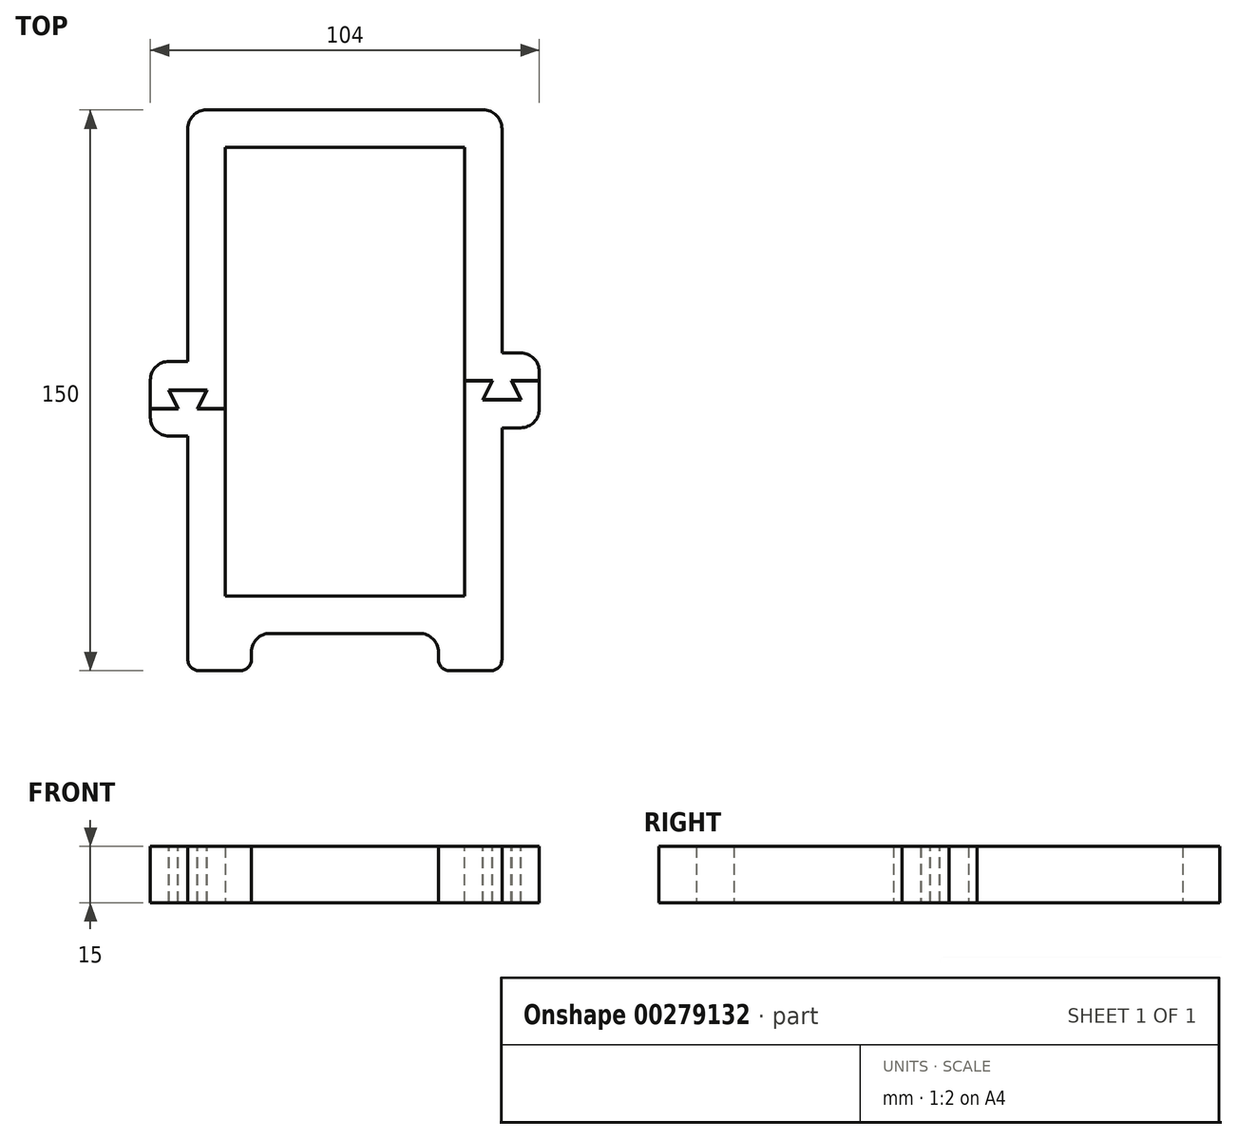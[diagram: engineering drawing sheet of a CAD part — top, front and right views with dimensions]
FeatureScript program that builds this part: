
annotation { "Feature Type Name" : "Feature", "Feature Type Description" : "" }
export const myFeature = defineFeature(function(context is Context, id is Id, definition is map)
    precondition{}
    {
        {
            var Q0;
            Q0=qCreatedBy(makeId("Top.planeOp"),FACE);
            var sketch = newSketch(context, id + "F0", { "sketchPlane" : qUnion([Q0])});
            skLineSegment(sketch, "E0.bottom", {"start": v(42, 75) * mm, "end": v(-42, 75) * mm});
            skLineSegment(sketch, "E0.left", {"start": v(42, 75) * mm, "end": v(42, -75) * mm});
            skLineSegment(sketch, "E0.right", {"start": v(-42, 75) * mm, "end": v(-42, -75) * mm});
            skPoint(sketch, "E0.middle", {"position": v(0, 0) * mm});
            skLineSegment(sketch, "E1.bottom", {"start": v(-32, 65) * mm, "end": v(32, 65) * mm});
            skLineSegment(sketch, "E1.top", {"start": v(-32, -55) * mm, "end": v(32, -55) * mm});
            skLineSegment(sketch, "E1.left", {"start": v(-32, 65) * mm, "end": v(-32, -55) * mm});
            skLineSegment(sketch, "E1.right", {"start": v(32, 65) * mm, "end": v(32, -55) * mm});
            skLineSegment(sketch, "E2.top", {"start": v(-25, -65) * mm, "end": v(25, -65) * mm});
            skLineSegment(sketch, "E2.left", {"start": v(-25, -75) * mm, "end": v(-25, -65) * mm});
            skLineSegment(sketch, "E2.right", {"start": v(25, -75) * mm, "end": v(25, -65) * mm});
            skLineSegment(sketch, "E3", {"start": v(-42, -75) * mm, "end": v(-25, -75) * mm});
            skLineSegment(sketch, "E4", {"start": v(25, -75) * mm, "end": v(42, -75) * mm});
            skSolve(sketch);
        }
        {
            var Q0;
            Q0=makeQuery(id+"F0.imprint","IMPRINT",FACE,{"disambiguationData":[TD([[makeQuery(id+"F0.imprint","IMPRINT",EDGE,{"derivedFrom":sQuery(id+"F0.wireOp",EDGE,"E0.bottom")}),1.0]])]});
            extrude(context, id + "F1", {"entities" : qUnion([Q0]), "depth" : 15 * mm});
        }
        {
            var Q0;
            Q0=makeQuery(id+"F1.opExtrude","SWEPT_EDGE",EDGE,{"disambiguationData":[OSD([sQuery(id+"F0.wireOp",EDGE,"E2.right"),sQuery(id+"F0.wireOp",EDGE,"E4")])]});
            var Q1;
            Q1=makeQuery(id+"F1.opExtrude","SWEPT_EDGE",EDGE,{"disambiguationData":[OSD([sQuery(id+"F0.wireOp",EDGE,"E0.left"),sQuery(id+"F0.wireOp",EDGE,"E4")])]});
            var Q2;
            Q2=makeQuery(id+"F1.opExtrude","SWEPT_EDGE",EDGE,{"disambiguationData":[OSD([sQuery(id+"F0.wireOp",EDGE,"E2.left"),sQuery(id+"F0.wireOp",EDGE,"E3")])]});
            var Q3;
            Q3=makeQuery(id+"F1.opExtrude","SWEPT_EDGE",EDGE,{"disambiguationData":[OSD([sQuery(id+"F0.wireOp",EDGE,"E0.right"),sQuery(id+"F0.wireOp",EDGE,"E3")])]});
            fillet(context, id + "F2", {"entities" : qUnion([Q0, Q1, Q2, Q3]), "radius" : 3 * mm, "tangentPropagation" : true, "allowEdgeOverflow" : false});
        }
        {
            var Q0;
            Q0=makeQuery(id+"F1.opExtrude","SWEPT_EDGE",EDGE,{"disambiguationData":[OSD([sQuery(id+"F0.wireOp",EDGE,"E2.top"),sQuery(id+"F0.wireOp",EDGE,"E2.left")])]});
            var Q1;
            Q1=makeQuery(id+"F1.opExtrude","SWEPT_EDGE",EDGE,{"disambiguationData":[OSD([sQuery(id+"F0.wireOp",EDGE,"E2.top"),sQuery(id+"F0.wireOp",EDGE,"E2.right")])]});
            var Q2;
            Q2=makeQuery(id+"F1.opExtrude","SWEPT_EDGE",EDGE,{"disambiguationData":[OSD([sQuery(id+"F0.wireOp",EDGE,"E0.bottom"),sQuery(id+"F0.wireOp",EDGE,"E0.right")])]});
            var Q3;
            Q3=makeQuery(id+"F1.opExtrude","SWEPT_EDGE",EDGE,{"disambiguationData":[OSD([sQuery(id+"F0.wireOp",EDGE,"E0.bottom"),sQuery(id+"F0.wireOp",EDGE,"E0.left")])]});
            fillet(context, id + "F3", {"entities" : qUnion([Q0, Q1, Q2, Q3]), "radius" : 5 * mm, "tangentPropagation" : true, "allowEdgeOverflow" : false});
        }
        {
            var Q0;
            Q0=makeQuery(id+"F1.opExtrude","SWEPT_FACE",FACE,{"disambiguationData":[OSD([sQuery(id+"F0.wireOp",EDGE,"E0.right")])]});
            var sketch = newSketch(context, id + "F4", { "sketchPlane" : qUnion([Q0])});
            skLineSegment(sketch, "E5.bottom", {"start": v(12.24, 15) * mm, "end": v(-7.76, 15) * mm});
            skLineSegment(sketch, "E5.top", {"start": v(12.24, 0) * mm, "end": v(-7.76, 0) * mm});
            skLineSegment(sketch, "E5.left", {"start": v(12.24, 15) * mm, "end": v(12.24, 0) * mm});
            skLineSegment(sketch, "E5.right", {"start": v(-7.76, 15) * mm, "end": v(-7.76, 0) * mm});
            skSolve(sketch);
        }
        {
            var Q0;
            Q0=makeQuery(id+"F4.imprint","IMPRINT",FACE,{"disambiguationData":[TD([[makeQuery(id+"F4.imprint","IMPRINT",EDGE,{"derivedFrom":sQuery(id+"F4.wireOp",EDGE,"E5.bottom")}),-1.0]])]});
            extrude(context, id + "F5", {"entities" : qUnion([Q0]), "operationType" : NewBodyOperationType.ADD, "depth" : 10 * mm});
        }
        {
            var Q0;
            Q0=makeQuery(id+"F1.opExtrude","SWEPT_FACE",FACE,{"disambiguationData":[OSD([sQuery(id+"F0.wireOp",EDGE,"E0.left")])]});
            var sketch = newSketch(context, id + "F6", { "sketchPlane" : qUnion([Q0])});
            skLineSegment(sketch, "E6.bottom", {"start": v(10, 15) * mm, "end": v(-10, 15) * mm});
            skLineSegment(sketch, "E6.top", {"start": v(10, 0) * mm, "end": v(-10, 0) * mm});
            skLineSegment(sketch, "E6.left", {"start": v(10, 15) * mm, "end": v(10, 0) * mm});
            skLineSegment(sketch, "E6.right", {"start": v(-10, 15) * mm, "end": v(-10, 0) * mm});
            skSolve(sketch);
        }
        {
            var Q0;
            Q0=makeQuery(id+"F6.imprint","IMPRINT",FACE,{"disambiguationData":[TD([[makeQuery(id+"F6.imprint","IMPRINT",EDGE,{"derivedFrom":sQuery(id+"F6.wireOp",EDGE,"E6.bottom")}),1.0]])]});
            extrude(context, id + "F7", {"entities" : qUnion([Q0]), "operationType" : NewBodyOperationType.ADD, "depth" : 10 * mm});
        }
        {
            var Q0;
            Q0=makeQuery(id+"F7.boolean.opBoolean","MERGE",FACE,{"derivedFrom":[makeQuery(id+"F5.boolean.opBoolean","MERGE",FACE,{"derivedFrom":[makeQuery(id+"F1.opExtrude","CAP_FACE",FACE,{"disambiguationData":[OSD([sQuery(id+"F0.wireOp",EDGE,"E0.bottom"),sQuery(id+"F0.wireOp",EDGE,"E0.left"),sQuery(id+"F0.wireOp",EDGE,"E0.right"),sQuery(id+"F0.wireOp",EDGE,"E1.bottom"),sQuery(id+"F0.wireOp",EDGE,"E1.top"),sQuery(id+"F0.wireOp",EDGE,"E1.left"),sQuery(id+"F0.wireOp",EDGE,"E1.right"),sQuery(id+"F0.wireOp",EDGE,"E2.top"),sQuery(id+"F0.wireOp",EDGE,"E2.left"),sQuery(id+"F0.wireOp",EDGE,"E2.right"),sQuery(id+"F0.wireOp",EDGE,"E3"),sQuery(id+"F0.wireOp",EDGE,"E4")])],"isStart":false}),makeQuery(id+"F5.opExtrude","SWEPT_FACE",FACE,{"disambiguationData":[OSD([sQuery(id+"F4.wireOp",EDGE,"E5.bottom")])]})]}),makeQuery(id+"F7.opExtrude","SWEPT_FACE",FACE,{"disambiguationData":[OSD([sQuery(id+"F6.wireOp",EDGE,"E6.bottom")])]})]});
            var sketch = newSketch(context, id + "F8", { "sketchPlane" : qUnion([Q0])});
            skLineSegment(sketch, "E7", {"start": v(-47, 0) * mm, "end": v(-37, 0) * mm});
            skLineSegment(sketch, "E8", {"start": v(-37, 0) * mm, "end": v(-39.5, -5) * mm});
            skLineSegment(sketch, "E9", {"start": v(-39.5, -5) * mm, "end": v(-31.78, -5) * mm});
            skLineSegment(sketch, "E10", {"start": v(-47, 0) * mm, "end": v(-44.5, -5) * mm});
            skLineSegment(sketch, "E11", {"start": v(-44.5, -5) * mm, "end": v(-53.27, -5) * mm});
            skLineSegment(sketch, "E12", {"start": v(-53.27, -5) * mm, "end": v(-53.27, -4.9) * mm});
            skLineSegment(sketch, "E13", {"start": v(-53.27, -4.9) * mm, "end": v(-44.66, -4.9) * mm});
            skLineSegment(sketch, "E14", {"start": v(-44.66, -4.9) * mm, "end": v(-47.16, 0.1) * mm});
            skLineSegment(sketch, "E15", {"start": v(-47.16, 0.1) * mm, "end": v(-36.84, 0.1) * mm});
            skLineSegment(sketch, "E16", {"start": v(-36.84, 0.1) * mm, "end": v(-39.34, -4.9) * mm});
            skLineSegment(sketch, "E17", {"start": v(-39.34, -4.9) * mm, "end": v(-31.19, -4.9) * mm});
            skLineSegment(sketch, "E18", {"start": v(-31.19, -4.9) * mm, "end": v(-31.19, -5) * mm});
            skLineSegment(sketch, "E19", {"start": v(-31.19, -5) * mm, "end": v(-31.78, -5) * mm});
            skLineSegment(sketch, "E20.MirrorCS", {"start": v(52.81, 2.5) * mm, "end": v(52.81, 2.6) * mm});
            skLineSegment(sketch, "E21.MirrorCS", {"start": v(30.73, 2.6) * mm, "end": v(30.73, 2.5) * mm});
            skLineSegment(sketch, "E22.MirrorCS", {"start": v(36.84, -2.5) * mm, "end": v(47.16, -2.5) * mm});
            skLineSegment(sketch, "E23.MirrorCS", {"start": v(39.5, 2.6) * mm, "end": v(30.73, 2.6) * mm});
            skLineSegment(sketch, "E24.MirrorCS", {"start": v(39.34, 2.5) * mm, "end": v(36.84, -2.5) * mm});
            skLineSegment(sketch, "E25.MirrorCS", {"start": v(44.66, 2.5) * mm, "end": v(52.81, 2.5) * mm});
            skLineSegment(sketch, "E26.MirrorCS", {"start": v(30.73, 2.5) * mm, "end": v(39.34, 2.5) * mm});
            skLineSegment(sketch, "E27.MirrorCS", {"start": v(44.5, 2.6) * mm, "end": v(52.81, 2.6) * mm});
            skLineSegment(sketch, "E28.MirrorCS", {"start": v(47.16, -2.5) * mm, "end": v(44.66, 2.5) * mm});
            skLineSegment(sketch, "E29.MirrorCS", {"start": v(47, -2.4) * mm, "end": v(44.5, 2.6) * mm});
            skLineSegment(sketch, "E30.MirrorCS", {"start": v(37, -2.4) * mm, "end": v(39.5, 2.6) * mm});
            skLineSegment(sketch, "E31.MirrorCS", {"start": v(37, -2.4) * mm, "end": v(47, -2.4) * mm});
            skSolve(sketch);
        }
        {
            var Q0;
            Q0 = qSketchRegion(id + "F8", true);
            extrude(context, id + "F9", {"entities" : qUnion([Q0]), "operationType" : NewBodyOperationType.REMOVE, "endBound" : BoundingType.THROUGH_ALL, "oppositeDirection" : true, "depth" : 25 * mm, "hasSecondDirection" : true, "secondDirectionBound" : SecondDirectionBoundingType.THROUGH_ALL, "secondDirectionOppositeDirection" : false, "secondDirectionDepth" : 25 * mm});
        }
        {
            var Q0;
            Q0=makeQuery(id+"F7.opExtrude","CAP_EDGE",EDGE,{"disambiguationData":[OSD([sQuery(id+"F6.wireOp",EDGE,"E6.right")])],"isStart":false});
            var Q1;
            Q1=makeQuery(id+"F7.opExtrude","CAP_EDGE",EDGE,{"disambiguationData":[OSD([sQuery(id+"F6.wireOp",EDGE,"E6.left")])],"isStart":false});
            var Q2;
            Q2=makeQuery(id+"F5.opExtrude","CAP_EDGE",EDGE,{"disambiguationData":[OSD([sQuery(id+"F4.wireOp",EDGE,"E5.right")])],"isStart":false});
            var Q3;
            Q3=makeQuery(id+"F5.opExtrude","CAP_EDGE",EDGE,{"disambiguationData":[OSD([sQuery(id+"F4.wireOp",EDGE,"E5.left")])],"isStart":false});
            fillet(context, id + "F10", {"entities" : qUnion([Q0, Q1, Q2, Q3]), "radius" : 5 * mm, "tangentPropagation" : true, "allowEdgeOverflow" : false});
        }
    });
